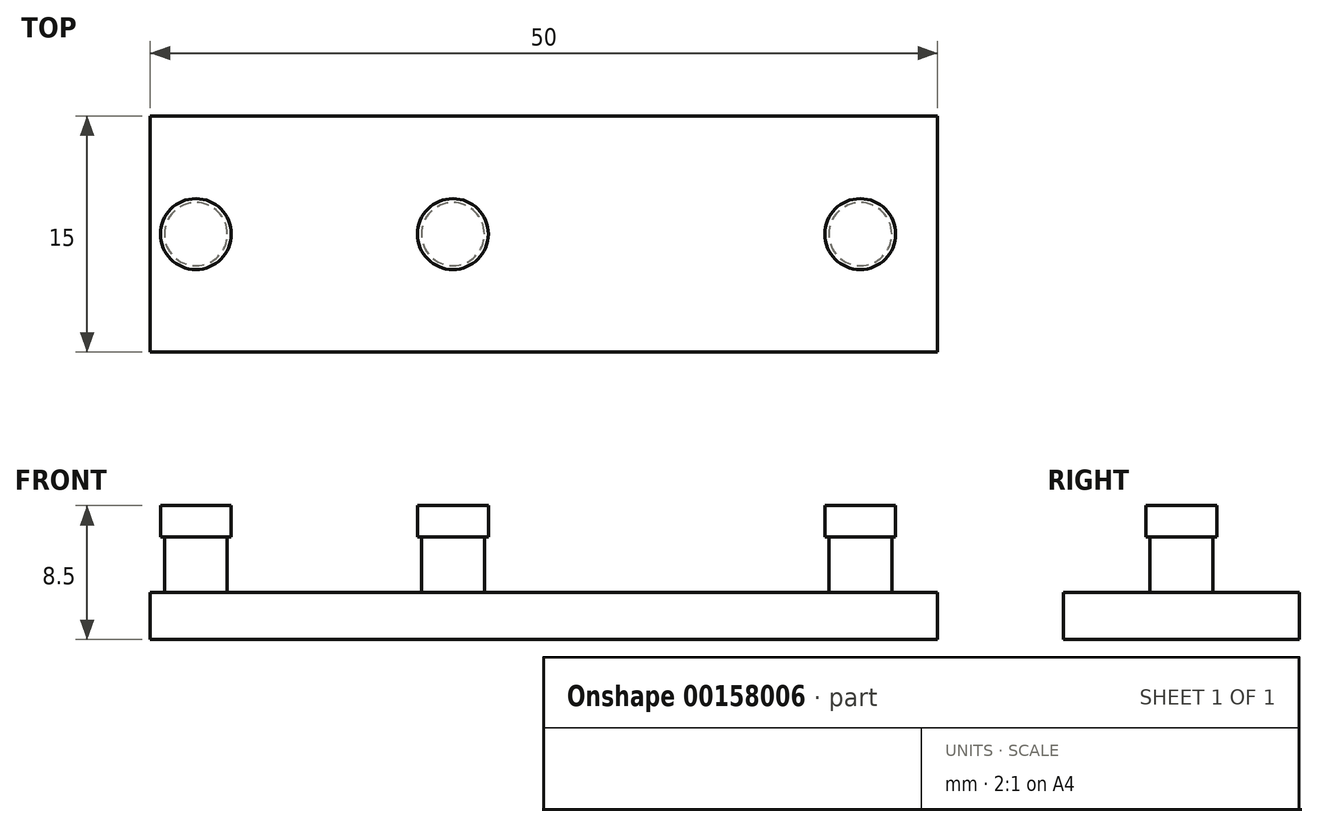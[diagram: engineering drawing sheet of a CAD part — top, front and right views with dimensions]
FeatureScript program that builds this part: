
annotation { "Feature Type Name" : "Feature", "Feature Type Description" : "" }
export const myFeature = defineFeature(function(context is Context, id is Id, definition is map)
    precondition{}
    {
        {
            var Q0;
            Q0=qCreatedBy(makeId("Top.planeOp"),FACE);
            var sketch = newSketch(context, id + "F0", { "sketchPlane" : qUnion([Q0])});
            skCircle(sketch, "E0", {"center": v(0, 0) * mm, "radius": 2 * mm});
            skLineSegment(sketch, "E1.bottom", {"start": v(-2.9, 7.5) * mm, "end": v(47.1, 7.5) * mm});
            skLineSegment(sketch, "E1.top", {"start": v(-2.9, -7.5) * mm, "end": v(47.1, -7.5) * mm});
            skLineSegment(sketch, "E1.left", {"start": v(-2.9, 7.5) * mm, "end": v(-2.9, -7.5) * mm});
            skLineSegment(sketch, "E1.right", {"start": v(47.1, 7.5) * mm, "end": v(47.1, -7.5) * mm});
            skCircle(sketch, "E2", {"center": v(16.32, 0) * mm, "radius": 2 * mm});
            skCircle(sketch, "E3", {"center": v(42.2, 0) * mm, "radius": 2 * mm});
            skSolve(sketch);
        }
        {
            var Q0;
            Q0=makeQuery(id+"F0.imprint","IMPRINT",FACE,{"disambiguationData":[TD([[makeQuery(id+"F0.imprint","IMPRINT",EDGE,{"derivedFrom":sQuery(id+"F0.wireOp",EDGE,"E0")}),-1.0]])]});
            extrude(context, id + "F1", {"entities" : qUnion([Q0]), "depth" : 3 * mm});
        }
        {
            var Q0;
            Q0=makeQuery(id+"F0.imprint","IMPRINT",FACE,{"disambiguationData":[TD([[makeQuery(id+"F0.imprint","IMPRINT",EDGE,{"derivedFrom":sQuery(id+"F0.wireOp",EDGE,"E0")}),1.0]])]});
            var Q1;
            Q1=makeQuery(id+"F0.imprint","IMPRINT",FACE,{"disambiguationData":[TD([[makeQuery(id+"F0.imprint","IMPRINT",EDGE,{"derivedFrom":sQuery(id+"F0.wireOp",EDGE,"E2")}),1.0]])]});
            var Q2;
            Q2=makeQuery(id+"F0.imprint","IMPRINT",FACE,{"disambiguationData":[TD([[makeQuery(id+"F0.imprint","IMPRINT",EDGE,{"derivedFrom":sQuery(id+"F0.wireOp",EDGE,"E3")}),1.0]])]});
            extrude(context, id + "F2", {"entities" : qUnion([Q0, Q1, Q2]), "operationType" : NewBodyOperationType.ADD, "depth" : 6.5 * mm});
        }
        {
            var Q0;
            Q0=makeQuery(id+"F2.opExtrude","CAP_FACE",FACE,{"disambiguationData":[OSD([sQuery(id+"F0.wireOp",EDGE,"E0")])],"isStart":false});
            var sketch = newSketch(context, id + "F3", { "sketchPlane" : qUnion([Q0])});
            skCircle(sketch, "E4.0", {"center": v(0, 0) * mm, "radius": 2 * mm});
            skCircle(sketch, "E5.0", {"center": v(16.32, 0) * mm, "radius": 2 * mm});
            skCircle(sketch, "E6.0", {"center": v(42.2, 0) * mm, "radius": 2 * mm});
            skCircle(sketch, "E7", {"center": v(0, 0) * mm, "radius": 2.25 * mm});
            skCircle(sketch, "E8", {"center": v(16.32, 0) * mm, "radius": 2.25 * mm});
            skCircle(sketch, "E9", {"center": v(42.2, 0) * mm, "radius": 2.25 * mm});
            skSolve(sketch);
        }
        {
            var Q0;
            Q0=makeQuery(id+"F3.imprint","IMPRINT",FACE,{"disambiguationData":[TD([[makeQuery(id+"F3.imprint","IMPRINT",EDGE,{"derivedFrom":sQuery(id+"F3.wireOp",EDGE,"E4.0")}),-1.0]])]});
            var Q1;
            Q1=makeQuery(id+"F3.imprint","IMPRINT",FACE,{"disambiguationData":[TD([[makeQuery(id+"F3.imprint","IMPRINT",EDGE,{"derivedFrom":sQuery(id+"F3.wireOp",EDGE,"E5.0")}),-1.0]])]});
            var Q2;
            Q2=makeQuery(id+"F3.imprint","IMPRINT",FACE,{"disambiguationData":[TD([[makeQuery(id+"F3.imprint","IMPRINT",EDGE,{"derivedFrom":sQuery(id+"F3.wireOp",EDGE,"E6.0")}),-1.0]])]});
            var Q3;
            Q3=makeQuery(id+"F3.imprint","IMPRINT",FACE,{"disambiguationData":[TD([[makeQuery(id+"F3.imprint","IMPRINT",EDGE,{"derivedFrom":sQuery(id+"F3.wireOp",EDGE,"E4.0")}),1.0]])]});
            var Q4;
            Q4=makeQuery(id+"F3.imprint","IMPRINT",FACE,{"disambiguationData":[TD([[makeQuery(id+"F3.imprint","IMPRINT",EDGE,{"derivedFrom":sQuery(id+"F3.wireOp",EDGE,"E5.0")}),1.0]])]});
            var Q5;
            Q5=makeQuery(id+"F3.imprint","IMPRINT",FACE,{"disambiguationData":[TD([[makeQuery(id+"F3.imprint","IMPRINT",EDGE,{"derivedFrom":sQuery(id+"F3.wireOp",EDGE,"E6.0")}),1.0]])]});
            extrude(context, id + "F4", {"entities" : qUnion([Q0, Q1, Q2, Q3, Q4, Q5]), "depth" : 2 * mm});
        }
    });
